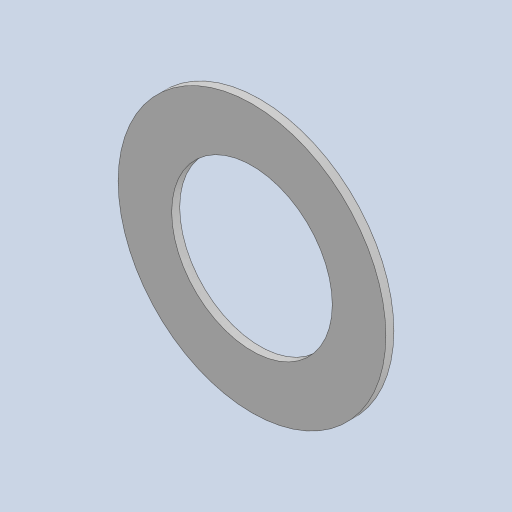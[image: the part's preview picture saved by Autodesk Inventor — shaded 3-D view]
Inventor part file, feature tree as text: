
AUTODESK INVENTOR PART (.ipt)
format: ipt  version: 2023 (Build 270158000, 158)  size: 113,664 bytes
history: native  units: mm
features: extrude x1, sketch x1
ambient origin geometry x8: Origin, YZ Plane, XZ Plane, XY Plane, X Axis, Y Axis, Z Axis, Center Point
bodies: Solid1 (feature_tree)
feature tree (2):
  extrude  "Extrusion1"  [1 undecoded]
  sketch  "Sketch_1"  dims[d0=0.3mm d1=0.0mm]
note: 1 required parameter value undecoded (feature->parameter linkage not recoverable at this tier; creation-order binding heuristic only, values carry confidence <= 0.55)
